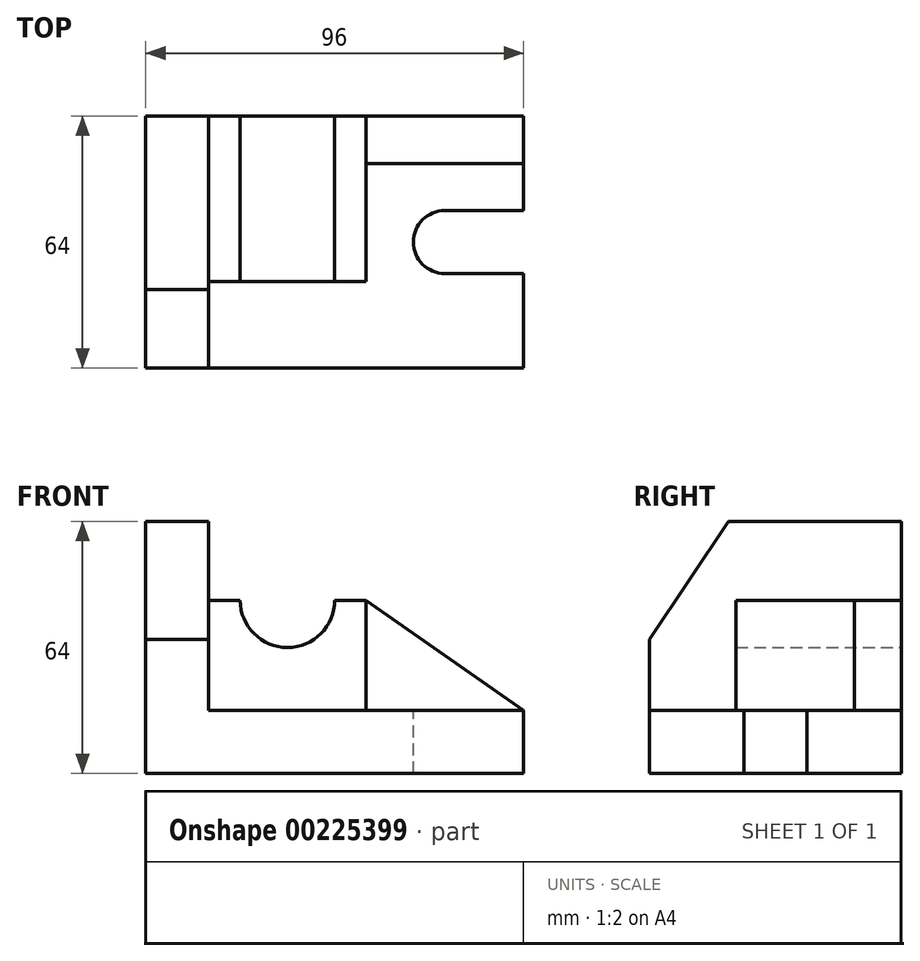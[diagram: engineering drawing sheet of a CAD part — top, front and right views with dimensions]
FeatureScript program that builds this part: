
annotation { "Feature Type Name" : "Feature", "Feature Type Description" : "" }
export const myFeature = defineFeature(function(context is Context, id is Id, definition is map)
    precondition{}
    {
        {
            var Q0;
            Q0=qCreatedBy(makeId("Top.planeOp"),FACE);
            var sketch = newSketch(context, id + "F0", { "sketchPlane" : qUnion([Q0])});
            skLineSegment(sketch, "E0.bottom", {"start": v(48, -32) * mm, "end": v(-48, -32) * mm});
            skLineSegment(sketch, "E0.top", {"start": v(48, 32) * mm, "end": v(-48, 32) * mm});
            skLineSegment(sketch, "E0.left", {"start": v(48, -32) * mm, "end": v(48, 32) * mm});
            skLineSegment(sketch, "E0.right", {"start": v(-48, -32) * mm, "end": v(-48, 32) * mm});
            skPoint(sketch, "E0.middle", {"position": v(0, 0) * mm});
            skSolve(sketch);
        }
        {
            var Q0;
            Q0 = qSketchRegion(id + "F0", true);
            extrude(context, id + "F1", {"entities" : qUnion([Q0]), "depth" : 16 * mm});
        }
        {
            var Q0;
            Q0=makeQuery(id+"F1.opExtrude","SWEPT_FACE",FACE,{"disambiguationData":[OSD([sQuery(id+"F0.wireOp",EDGE,"E0.right")])]});
            var sketch = newSketch(context, id + "F2", { "sketchPlane" : qUnion([Q0])});
            skLineSegment(sketch, "E1.bottom", {"start": v(-32, 0) * mm, "end": v(32, 0) * mm});
            skLineSegment(sketch, "E1.top", {"start": v(-32, 64) * mm, "end": v(12, 64) * mm});
            skLineSegment(sketch, "E1.left", {"start": v(-32, 0) * mm, "end": v(-32, 64) * mm});
            skLineSegment(sketch, "E1.right", {"start": v(32, 0) * mm, "end": v(32, 34) * mm});
            skLineSegment(sketch, "E2", {"start": v(32, 34) * mm, "end": v(12, 64) * mm});
            skSolve(sketch);
        }
        {
            var Q0;
            Q0 = qSketchRegion(id + "F2", true);
            extrude(context, id + "F3", {"entities" : qUnion([Q0]), "operationType" : NewBodyOperationType.ADD, "oppositeDirection" : true, "depth" : 16 * mm});
        }
        {
            var Q0;
            Q0=makeQuery(id+"F3.boolean.opBoolean","MERGE",FACE,{"derivedFrom":[makeQuery(id+"F1.opExtrude","SWEPT_FACE",FACE,{"disambiguationData":[OSD([sQuery(id+"F0.wireOp",EDGE,"E0.top")])]}),makeQuery(id+"F3.opExtrude","SWEPT_FACE",FACE,{"disambiguationData":[OSD([sQuery(id+"F2.wireOp",EDGE,"E1.left")])]})]});
            var sketch = newSketch(context, id + "F4", { "sketchPlane" : qUnion([Q0])});
            skLineSegment(sketch, "E3.bottom", {"start": v(32, 16) * mm, "end": v(-8, 16) * mm});
            skLineSegment(sketch, "E3.top", {"start": v(32, 44) * mm, "end": v(24, 44) * mm});
            skLineSegment(sketch, "E3.left", {"start": v(32, 16) * mm, "end": v(32, 44) * mm});
            skLineSegment(sketch, "E3.right", {"start": v(-8, 16) * mm, "end": v(-8, 44) * mm});
            skArc(sketch, "E4", {"start": v(0, 44) * mm, "mid": v(12, 32) * mm, "end": v(24, 44) * mm});
            skLineSegment(sketch, "E5.trimOffspring", {"start": v(0, 44) * mm, "end": v(-8, 44) * mm});
            skSolve(sketch);
        }
        {
            var Q0;
            Q0 = qSketchRegion(id + "F4", true);
            extrude(context, id + "F5", {"entities" : qUnion([Q0]), "oppositeDirection" : true, "depth" : 42 * mm});
        }
        {
            var Q0;
            Q0=makeQuery(id+"F3.boolean.opBoolean","MERGE",FACE,{"derivedFrom":[makeQuery(id+"F1.opExtrude","SWEPT_FACE",FACE,{"disambiguationData":[OSD([sQuery(id+"F0.wireOp",EDGE,"E0.top")])]}),makeQuery(id+"F3.opExtrude","SWEPT_FACE",FACE,{"disambiguationData":[OSD([sQuery(id+"F2.wireOp",EDGE,"E1.left")])]})]});
            var sketch = newSketch(context, id + "F6", { "sketchPlane" : qUnion([Q0])});
            skLineSegment(sketch, "E6.bottom", {"start": v(-8, 16) * mm, "end": v(-48, 16) * mm});
            skLineSegment(sketch, "E6.left", {"start": v(-8, 16) * mm, "end": v(-8, 44) * mm});
            skLineSegment(sketch, "E7", {"start": v(-8, 44) * mm, "end": v(-48, 16) * mm});
            skSolve(sketch);
        }
        {
            var Q0;
            Q0=makeQuery(id+"F6.imprint","IMPRINT",FACE,{"disambiguationData":[TD([[makeQuery(id+"F6.imprint","IMPRINT",EDGE,{"derivedFrom":sQuery(id+"F6.wireOp",EDGE,"E6.bottom")}),1.0]])]});
            extrude(context, id + "F7", {"entities" : qUnion([Q0]), "oppositeDirection" : true, "depth" : 12 * mm});
        }
        {
            var Q0;
            Q0=makeQuery(id+"F1.opExtrude","CAP_FACE",FACE,{"disambiguationData":[OSD([sQuery(id+"F0.wireOp",EDGE,"E0.bottom"),sQuery(id+"F0.wireOp",EDGE,"E0.top"),sQuery(id+"F0.wireOp",EDGE,"E0.left"),sQuery(id+"F0.wireOp",EDGE,"E0.right")])],"isStart":false});
            var sketch = newSketch(context, id + "F8", { "sketchPlane" : qUnion([Q0])});
            skPoint(sketch, "E8.endSnap0", {"position": v(48, 0) * mm});
            skArc(sketch, "E9", {"start": v(28, 8) * mm, "mid": v(20, 0) * mm, "end": v(28, -8) * mm});
            skLineSegment(sketch, "E10", {"start": v(28, 8) * mm, "end": v(48, 8) * mm});
            skLineSegment(sketch, "E11", {"start": v(48, -8) * mm, "end": v(28, -8) * mm});
            skLineSegment(sketch, "E12", {"start": v(48, 8) * mm, "end": v(48, -8) * mm});
            skSolve(sketch);
        }
        {
            var Q0;
            Q0 = qSketchRegion(id + "F8", true);
            extrude(context, id + "F9", {"entities" : qUnion([Q0]), "operationType" : NewBodyOperationType.REMOVE, "oppositeDirection" : true, "depth" : 25 * mm});
        }
    });
